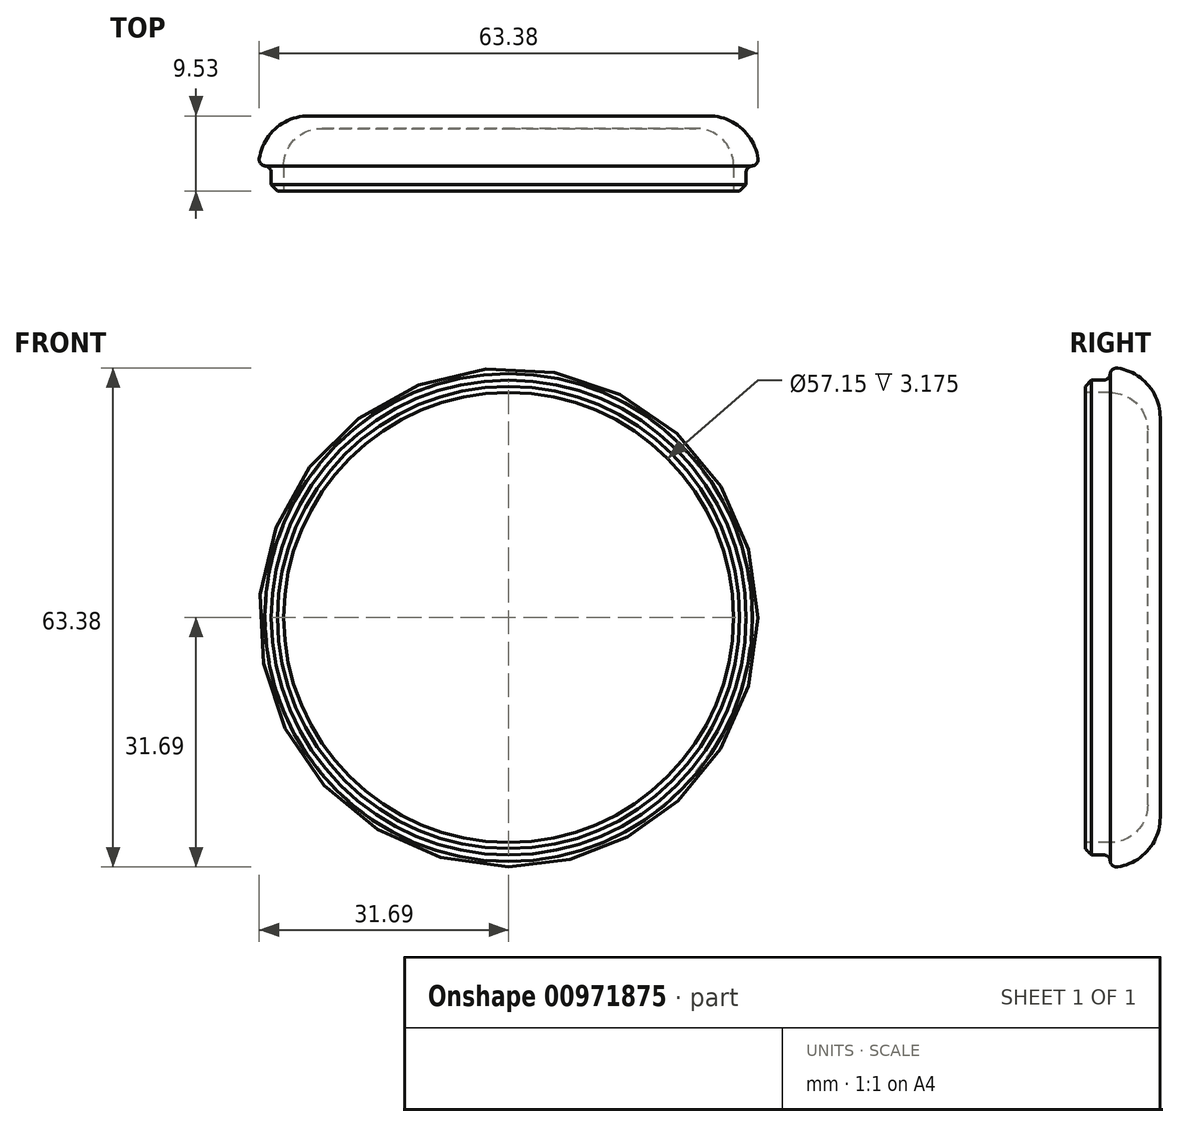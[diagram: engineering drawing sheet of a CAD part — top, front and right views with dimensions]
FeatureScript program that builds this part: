
annotation { "Feature Type Name" : "Feature", "Feature Type Description" : "" }
export const myFeature = defineFeature(function(context is Context, id is Id, definition is map)
    precondition{}
    {
        {
            var Q0;
            Q0=qCreatedBy(makeId("Top.planeOp"),FACE);
            var sketch = newSketch(context, id + "F0", { "sketchPlane" : qUnion([Q0])});
            skLineSegment(sketch, "E0", {"start": v(0, 0) * mm, "end": v(0, 1.59) * mm});
            skLineSegment(sketch, "E1", {"start": v(0, 19.05) * mm, "end": v(25.4, 19.05) * mm});
            skLineSegment(sketch, "E2", {"start": v(31.75, 12.7) * mm, "end": v(31.75, 9.53) * mm});
            skLineSegment(sketch, "E3", {"start": v(22.23, 0) * mm, "end": v(0, 0) * mm});
            skPoint(sketch, "E4.visualSharp", {"position": v(31.75, 19.05) * mm});
            skArc(sketch, "E4.filletArc", {"start": v(31.68, 13.65) * mm, "mid": v(29.54, 17.51) * mm, "end": v(25.4, 19.05) * mm});
            skPoint(sketch, "E5.visualSharp", {"position": v(31.75, 0) * mm});
            skArc(sketch, "E5.filletArc", {"start": v(22.23, 0) * mm, "mid": v(28.96, 2.79) * mm, "end": v(31.75, 9.53) * mm});
            skLineSegment(sketch, "E6.0", {"start": v(22.23, 1.59) * mm, "end": v(0, 1.59) * mm});
            skArc(sketch, "E6.1", {"start": v(22.23, 1.59) * mm, "mid": v(27.84, 3.91) * mm, "end": v(30.16, 9.53) * mm});
            skLineSegment(sketch, "E6.2", {"start": v(30.16, 11.87) * mm, "end": v(30.16, 9.53) * mm});
            skLineSegment(sketch, "E6.3", {"start": v(0, 17.46) * mm, "end": v(23.81, 17.46) * mm});
            skPoint(sketch, "E7.visualSharp", {"position": v(30.16, 17.46) * mm});
            skLineSegment(sketch, "E8.trimOffspring", {"start": v(0, 17.46) * mm, "end": v(0, 19.05) * mm});
            skLineSegment(sketch, "E9", {"start": v(30.86, 12.7) * mm, "end": v(30.99, 12.7) * mm});
            skLineSegment(sketch, "E10.0", {"start": v(28.58, 12.7) * mm, "end": v(28.58, 9.53) * mm});
            skLineSegment(sketch, "E11", {"start": v(28.58, 9.53) * mm, "end": v(30.16, 9.53) * mm});
            skArc(sketch, "E12.filletArc", {"start": v(28.58, 12.7) * mm, "mid": v(27.18, 16.07) * mm, "end": v(23.81, 17.46) * mm});
            skPoint(sketch, "E13.visualSharp", {"position": v(30.16, 12.7) * mm});
            skArc(sketch, "E13.filletArc", {"start": v(30.99, 12.7) * mm, "mid": v(30.4, 12.46) * mm, "end": v(30.16, 11.87) * mm});
            skPoint(sketch, "E14.visualSharp", {"position": v(31.75, 12.7) * mm});
            skArc(sketch, "E14.filletArc", {"start": v(30.86, 12.7) * mm, "mid": v(31.49, 12.99) * mm, "end": v(31.68, 13.65) * mm});
            skSolve(sketch);
        }
        {
            var Q0;
            Q0=makeQuery(id+"F0.imprint","IMPRINT",FACE,{"disambiguationData":[TD([[makeQuery(id+"F0.imprint","IMPRINT",EDGE,{"derivedFrom":sQuery(id+"F0.wireOp",EDGE,"E1")}),-1.0]])]});
            var Q1;
            Q1=sQuery(id+"F0.wireOp",EDGE,"E8.trimOffspring");
            revolve(context, id + "F1", {"surfaceOperationType" : NewSurfaceOperationType.NEW, "entities" : qUnion([Q0]), "axis" : qUnion([Q1]), "revolveType" : RevolveType.FULL});
        }
        {
            var Q0;
            Q0=makeQuery(id+"F1.opRevolve","SWEPT_EDGE",EDGE,{"disambiguationData":[OSD([sQuery(id+"F0.wireOp",EDGE,"E11"),sQuery(id+"F0.wireOp",EDGE,"E6.2")])]});
            chamfer(context, id + "F2", {"entities" : qUnion([Q0]), "width" : 0.81 * mm, "tangentPropagation" : true});
        }
    });
